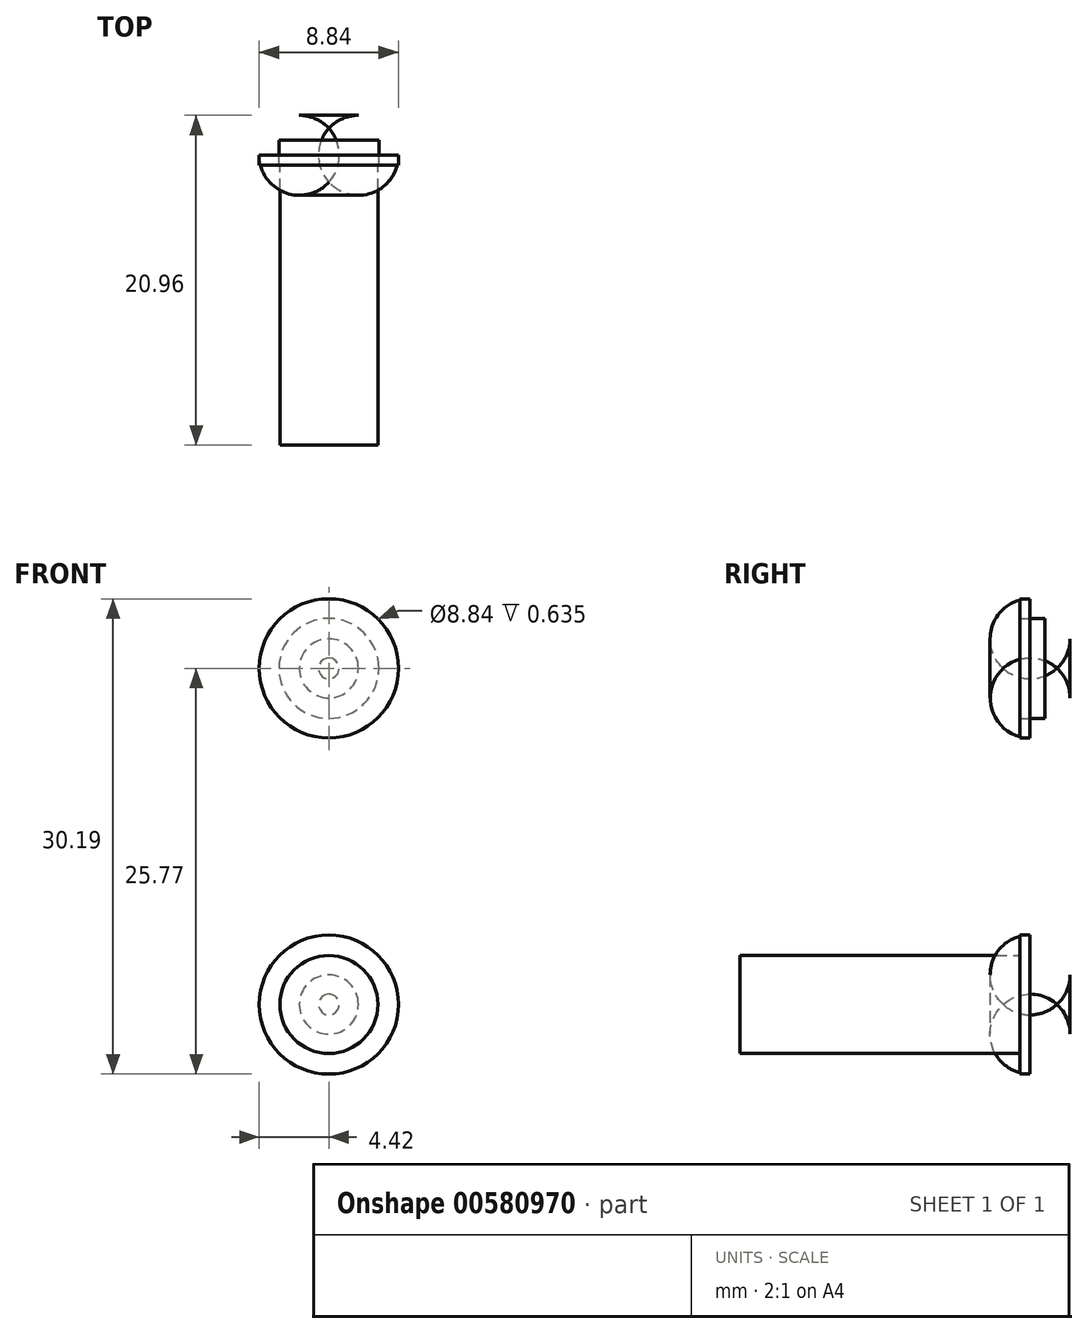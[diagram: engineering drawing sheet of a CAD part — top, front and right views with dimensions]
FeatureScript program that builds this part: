
annotation { "Feature Type Name" : "Feature", "Feature Type Description" : "" }
export const myFeature = defineFeature(function(context is Context, id is Id, definition is map)
    precondition{}
    {
        {
            var Q0;
            Q0=qCreatedBy(makeId("Front.planeOp"),FACE);
            var sketch = newSketch(context, id + "F0", { "sketchPlane" : qUnion([Q0])});
            skCircle(sketch, "E0", {"center": v(0, 0) * mm, "radius": 3.11 * mm});
            skCircle(sketch, "E1", {"center": v(0, 0) * mm, "radius": 4.42 * mm});
            skCircle(sketch, "E2", {"center": v(0, 21.35) * mm, "radius": 4.42 * mm});
            skCircle(sketch, "E3", {"center": v(0, 21.35) * mm, "radius": 3.18 * mm});
            skSolve(sketch);
        }
        {
            var Q0;
            Q0=makeQuery(id+"F0.imprint","IMPRINT",FACE,{"disambiguationData":[TD([[makeQuery(id+"F0.imprint","IMPRINT",EDGE,{"derivedFrom":sQuery(id+"F0.wireOp",EDGE,"E0")}),1.0]])]});
            extrude(context, id + "F1", {"entities" : qUnion([Q0]), "depth" : 20.95 * mm, "offsetDistance" : 25.4 * mm});
        }
        {
            var Q0;
            Q0=makeQuery(id+"F0.imprint","IMPRINT",FACE,{"disambiguationData":[TD([[makeQuery(id+"F0.imprint","IMPRINT",EDGE,{"derivedFrom":sQuery(id+"F0.wireOp",EDGE,"E0")}),-1.0]])]});
            extrude(context, id + "F2", {"entities" : qUnion([Q0]), "operationType" : NewBodyOperationType.ADD, "depth" : 3.17 * mm, "offsetDistance" : 25.4 * mm});
        }
        {
            var Q0;
            Q0=makeQuery(id+"F2.opExtrude","CAP_EDGE",EDGE,{"disambiguationData":[OSD([sQuery(id+"F0.wireOp",EDGE,"E1")])],"isStart":true});
            fillet(context, id + "F3", {"entities" : qUnion([Q0]), "radius" : 2.54 * mm, "tangentPropagation" : true, "allowEdgeOverflow" : false});
        }
        {
            var Q0;
            Q0=makeQuery(id+"F0.imprint","IMPRINT",FACE,{"disambiguationData":[TD([[makeQuery(id+"F0.imprint","IMPRINT",EDGE,{"derivedFrom":sQuery(id+"F0.wireOp",EDGE,"E2")}),1.0]])]});
            extrude(context, id + "F4", {"entities" : qUnion([Q0]), "depth" : 3.17 * mm, "offsetDistance" : 25.4 * mm});
        }
        {
            var Q0;
            Q0=makeQuery(id+"F0.imprint","IMPRINT",FACE,{"disambiguationData":[TD([[makeQuery(id+"F0.imprint","IMPRINT",EDGE,{"derivedFrom":sQuery(id+"F0.wireOp",EDGE,"E3")}),1.0]])]});
            extrude(context, id + "F5", {"entities" : qUnion([Q0]), "operationType" : NewBodyOperationType.ADD, "depth" : 1.59 * mm, "offsetDistance" : 25.4 * mm});
        }
        {
            var Q0;
            Q0=makeQuery(id+"F4.opExtrude","CAP_EDGE",EDGE,{"disambiguationData":[OSD([sQuery(id+"F0.wireOp",EDGE,"E2")])],"isStart":true});
            fillet(context, id + "F6", {"entities" : qUnion([Q0]), "radius" : 2.54 * mm, "tangentPropagation" : true, "allowEdgeOverflow" : false});
        }
    });
